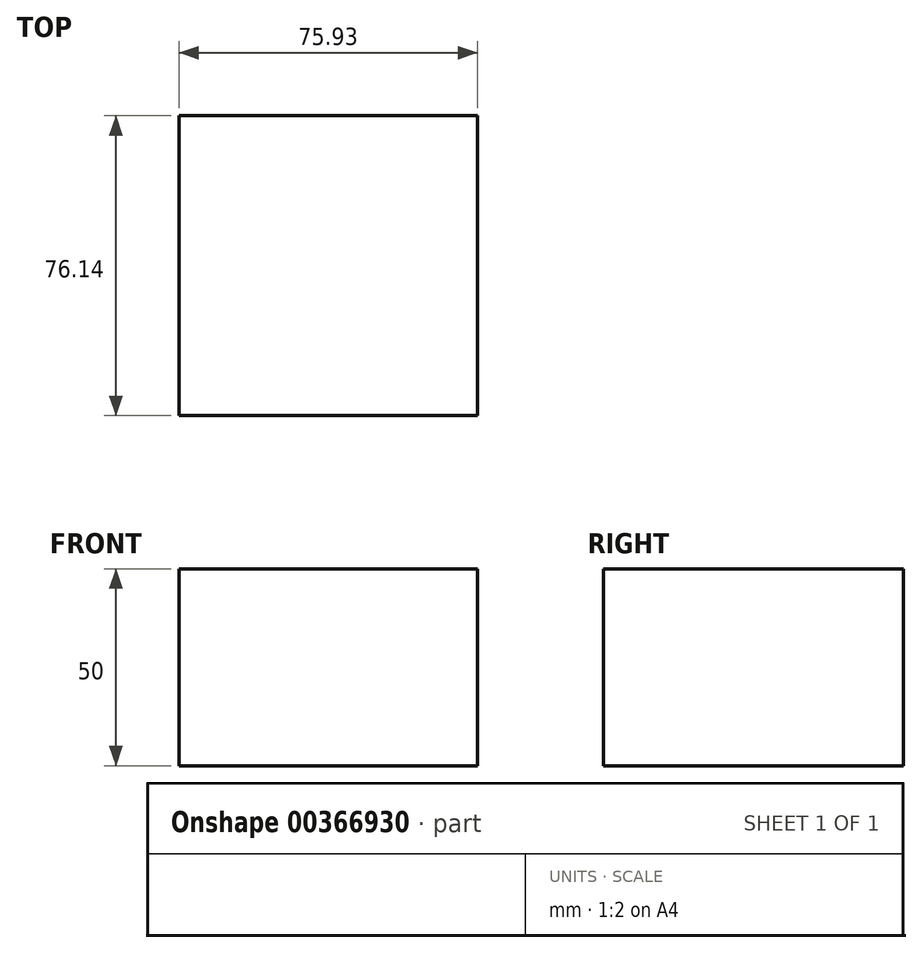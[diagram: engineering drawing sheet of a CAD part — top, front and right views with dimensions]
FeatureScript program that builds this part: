
annotation { "Feature Type Name" : "Feature", "Feature Type Description" : "" }
export const myFeature = defineFeature(function(context is Context, id is Id, definition is map)
    precondition{}
    {
        {
            var Q0;
            Q0=qCreatedBy(makeId("Top.planeOp"),FACE);
            var sketch = newSketch(context, id + "F0", { "sketchPlane" : qUnion([Q0])});
            skLineSegment(sketch, "E0.bottom", {"start": v(0, 0) * mm, "end": v(75.93, 0) * mm});
            skLineSegment(sketch, "E0.top", {"start": v(0, -76.14) * mm, "end": v(75.93, -76.14) * mm});
            skLineSegment(sketch, "E0.left", {"start": v(0, 0) * mm, "end": v(0, -76.14) * mm});
            skLineSegment(sketch, "E0.right", {"start": v(75.93, 0) * mm, "end": v(75.93, -76.14) * mm});
            skSolve(sketch);
        }
        {
            var Q0;
            Q0=makeQuery(id+"F0.imprint","IMPRINT",FACE,{"disambiguationData":[TD([[makeQuery(id+"F0.imprint","IMPRINT",EDGE,{"derivedFrom":sQuery(id+"F0.wireOp",EDGE,"E0.bottom")}),-1.0]])]});
            extrude(context, id + "F1", {"entities" : qUnion([Q0]), "depth" : 50 * mm});
        }
    });
